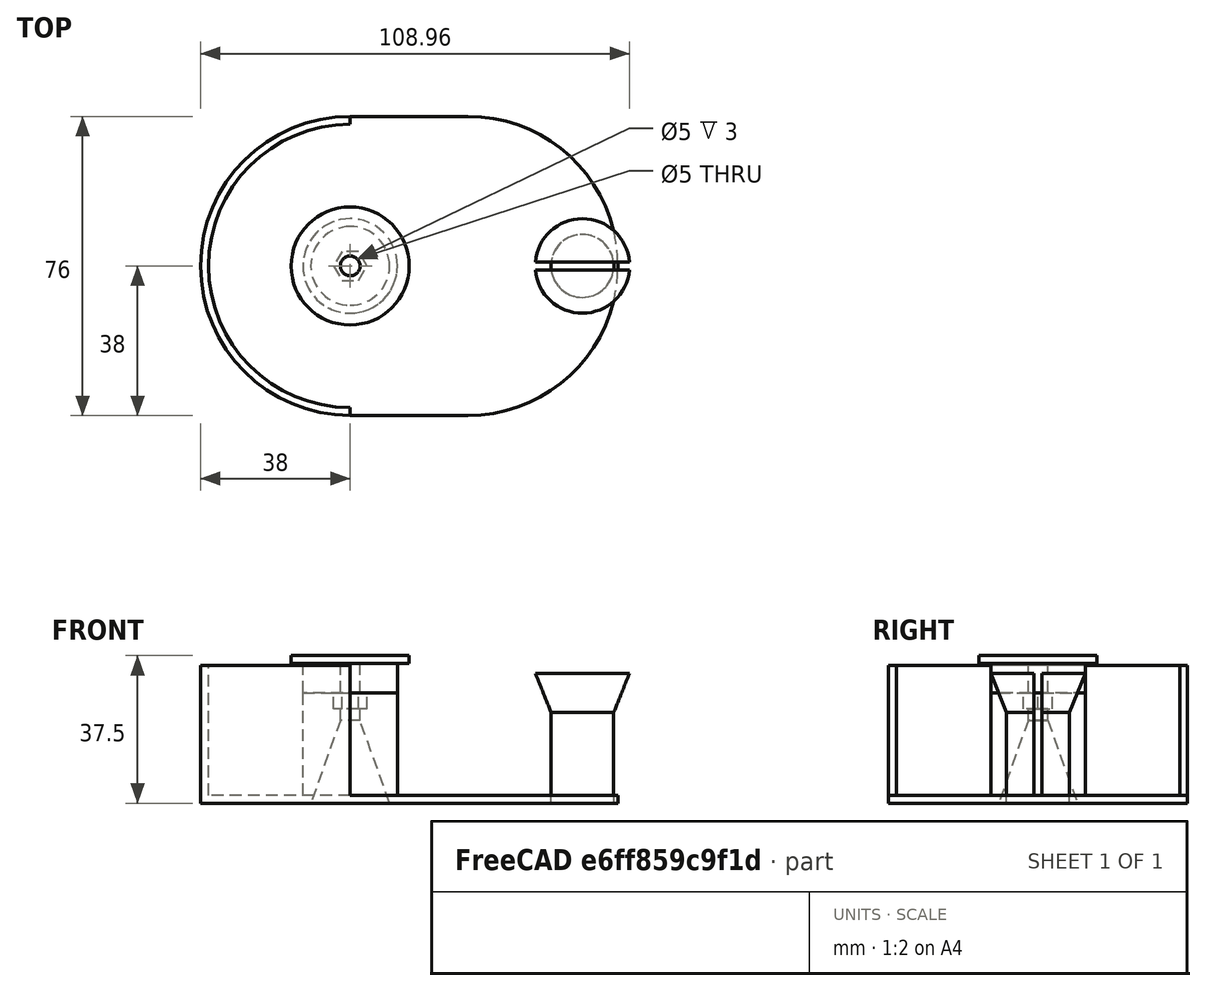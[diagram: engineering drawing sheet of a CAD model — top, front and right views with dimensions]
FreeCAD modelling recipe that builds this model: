
FCSTD DOCUMENT  (FreeCAD 0.18.4R)
Label: wire_drum_holder
License: All rights reserved
LicenseURL: http://en.wikipedia.org/wiki/All_rights_reserved
objects: Part::Cylinder×9, Part::Cut×4, Part::MultiFuse×4, Part::Box×2, Part::Cone×2, App::Part×2, Part::RegularPolygon×1, Part::Extrusion×1, Part::Compound×1
note: 24 computed .brp shape members not serialized (recipe doc carries the construction recipe); baked Part::Feature solids carry a one-line shape summary decoded from their .brp

FEATURE [Part::Cylinder] Cylinder  label="big cylinder"
  Angle = 180
  AttacherType = Attacher::AttachEngine3D
  Height = 35
  Placement = pos=(0,0,0) rot=(0,0,1;1.5708rad)
  Radius = 38
FEATURE [Part::Cylinder] Cylinder001  label="center cylinder"
  Angle = 360
  AttacherType = Attacher::AttachEngine3D
  Height = 28
  Radius = 12
FEATURE [Part::Box] Box  label="bottom cube"
  AttacherType = Attacher::AttachEngine3D
  Height = 2
  Length = 30
  Placement = pos=(0,-38,0) rot=(0,0,1;0rad)
  Width = 76
FEATURE [Part::Cylinder] Cylinder002  label="other wire cylinder"
  Angle = 360
  AttacherType = Attacher::AttachEngine3D
  Height = 32
  Placement = pos=(59,0,0) rot=(0,0,1;0rad)
  Radius = 8
FEATURE [Part::Cylinder] Cylinder003  label="extraction cylinder"
  Angle = 180
  AttacherType = Attacher::AttachEngine3D
  Height = 35
  Placement = pos=(0,0,2) rot=(0,0,1;1.5708rad)
  Radius = 36
FEATURE [Part::Cut] Cut  label="outer bottom cylinder cut"
  Base = -> Cylinder
  Tool = -> Cylinder003
FEATURE [Part::Cylinder] Cylinder004  label="center hole"
  Angle = 360
  AttacherType = Attacher::AttachEngine3D
  Height = 30
  Radius = 2.5
FEATURE [Part::Cone] Cone
  Angle = 360
  AttacherType = Attacher::AttachEngine3D
  Height = 21
  Radius1 = 10
  Radius2 = 2.5
FEATURE [Part::Cone] Cone001
  Angle = 360
  AttacherType = Attacher::AttachEngine3D
  Height = 10
  Placement = pos=(59,0,23) rot=(0,0,1;0rad)
  Radius1 = 8
  Radius2 = 12
FEATURE [Part::Box] Box001  label="cut cube"
  AttacherType = Attacher::AttachEngine3D
  Height = 35
  Length = 30
  Placement = pos=(43,-1,2) rot=(0,0,1;0rad)
  Width = 2
FEATURE [Part::MultiFuse] Fusion002  label="other wire fusion"
  Shapes = -> [Cone001,Cylinder002]
FEATURE [Part::Cut] Cut002  label="other wire cut"
  Base = -> Fusion002
  Tool = -> Box001
FEATURE [Part::RegularPolygon] RegularPolygon  label="Regular polygon"
  AttacherType = Attacher::AttachEngine3D
  Circumradius = 4.25
  Polygon = 6
FEATURE [Part::Extrusion] Extrude  label="nut extrude"
  Base = -> RegularPolygon
  Dir = (0,0,1)
  DirMode = 2
  FaceMakerClass = Part::FaceMakerBullseye
  LengthFwd = 4
  LengthRev = 0
  Placement = pos=(0,0,24) rot=(0,0,1;0rad)
  Solid = true
  Symmetric = false
FEATURE [Part::MultiFuse] Fusion  label="central hole fusion"
  Shapes = -> [Cylinder004,Cone,Extrude]
FEATURE [Part::Cylinder] Cylinder005  label="other side cylinder"
  Angle = 180
  AttacherType = Attacher::AttachEngine3D
  Height = 2
  Placement = pos=(30,-6.7e-15,0) rot=(0,0,1;4.71239rad)
  Radius = 38
FEATURE [Part::MultiFuse] Fusion001
  Shapes = -> [Cylinder001,Box,Cut,Cylinder005]
FEATURE [Part::Cut] Cut001  label="drum cut"
  Base = -> Fusion001
  Tool = -> Fusion
FEATURE [Part::Compound] Compound
  Links = -> [Cut001,Cut002]
FEATURE [App::Part] Part  label="bottom part"
  Group = -> [Box,Cylinder002,Cylinder,Cylinder001,Cut,Cylinder003,Fusion001,Fusion,Box001,Cone,Cylinder004,Cut001,Fusion002,Cone001,Cut002,Extrude,Cylinder005,RegularPolygon,Compound]
  Origin = -> Origin
FEATURE [Part::Cylinder] Cylinder006  label="top center cylinder"
  Angle = 360
  AttacherType = Attacher::AttachEngine3D
  Height = 9
  Placement = pos=(0,0,28) rot=(0,0,1;0rad)
  Radius = 12
FEATURE [Part::Cylinder] Cylinder007  label="top center hole"
  Angle = 360
  AttacherType = Attacher::AttachEngine3D
  Height = 30
  Placement = pos=(0,0,17) rot=(0,0,1;0rad)
  Radius = 2.5
FEATURE [Part::Cylinder] Cylinder008  label="top center top cylinder"
  Angle = 360
  AttacherType = Attacher::AttachEngine3D
  Height = 2
  Placement = pos=(0,0,35.5) rot=(0,0,1;0rad)
  Radius = 15
FEATURE [Part::MultiFuse] Fusion003  label="top cylinder fusion"
  Shapes = -> [Cylinder008,Cylinder006]
FEATURE [Part::Cut] Cut003  label="top part cut"
  Base = -> Fusion003
  Tool = -> Cylinder007
FEATURE [App::Part] Part001  label="top part"
  Group = -> [Cylinder006,Cylinder007,Cylinder008,Fusion003,Cut003]
  Origin = -> Origin001
